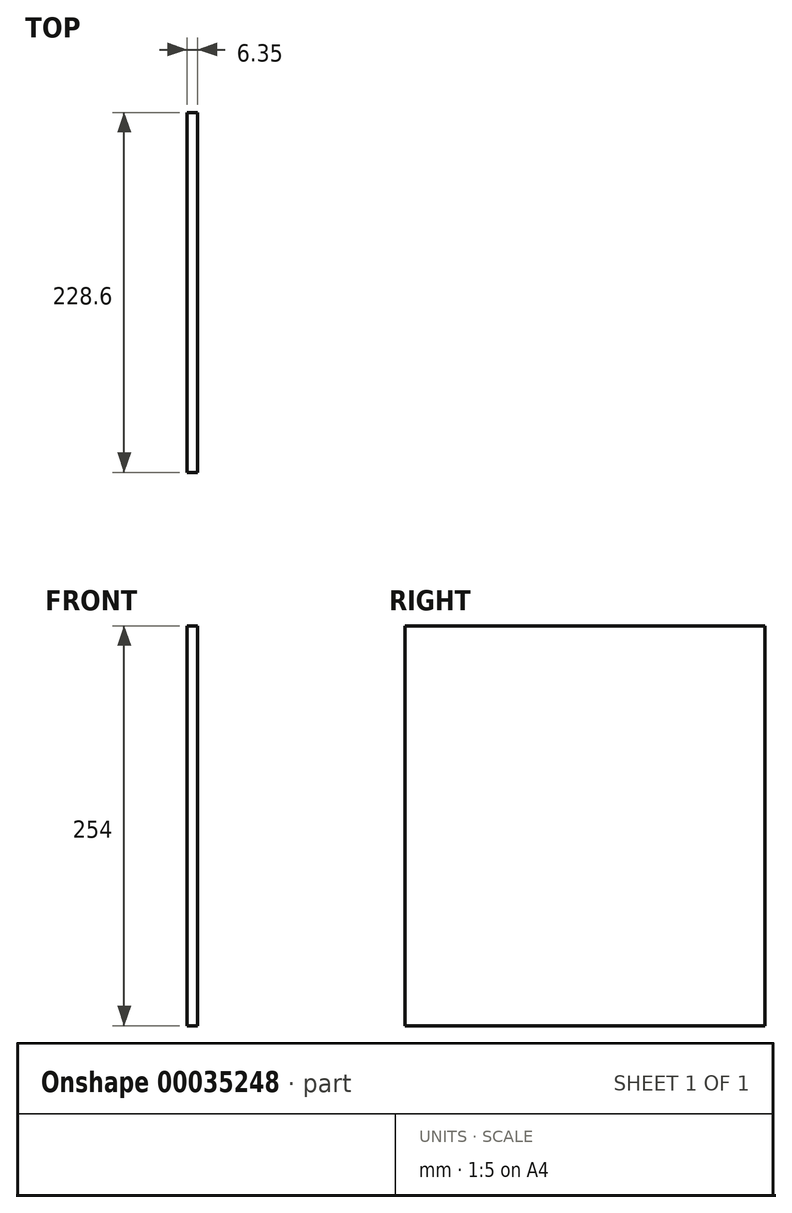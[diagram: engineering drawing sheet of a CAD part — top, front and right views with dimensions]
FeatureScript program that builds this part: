
annotation { "Feature Type Name" : "Feature", "Feature Type Description" : "" }
export const myFeature = defineFeature(function(context is Context, id is Id, definition is map)
    precondition{}
    {
        {
            var Q0;
            Q0=qCreatedBy(makeId("Right.planeOp"),FACE);
            var sketch = newSketch(context, id + "F0", { "sketchPlane" : qUnion([Q0])});
            skLineSegment(sketch, "E0.rect.bottom", {"start": v(114.3, -127) * mm, "end": v(-114.3, -127) * mm});
            skLineSegment(sketch, "E0.rect.top", {"start": v(114.3, 127) * mm, "end": v(-114.3, 127) * mm});
            skLineSegment(sketch, "E0.rect.left", {"start": v(114.3, -127) * mm, "end": v(114.3, 127) * mm});
            skLineSegment(sketch, "E0.rect.right", {"start": v(-114.3, -127) * mm, "end": v(-114.3, 127) * mm});
            skPoint(sketch, "E0.rect.middle", {"position": v(0, 0) * mm});
            skSolve(sketch);
        }
        {
            var Q0;
            Q0=makeQuery(id+"F0.imprint","IMPRINT",FACE,{"disambiguationData":[TD([[makeQuery(id+"F0.imprint","IMPRINT",EDGE,{"derivedFrom":sQuery(id+"F0.wireOp",EDGE,"E0.rect.bottom")}),-1.0]])]});
            extrude(context, id + "F1", {"entities" : qUnion([Q0]), "depth" : 6.35 * mm});
        }
    });
